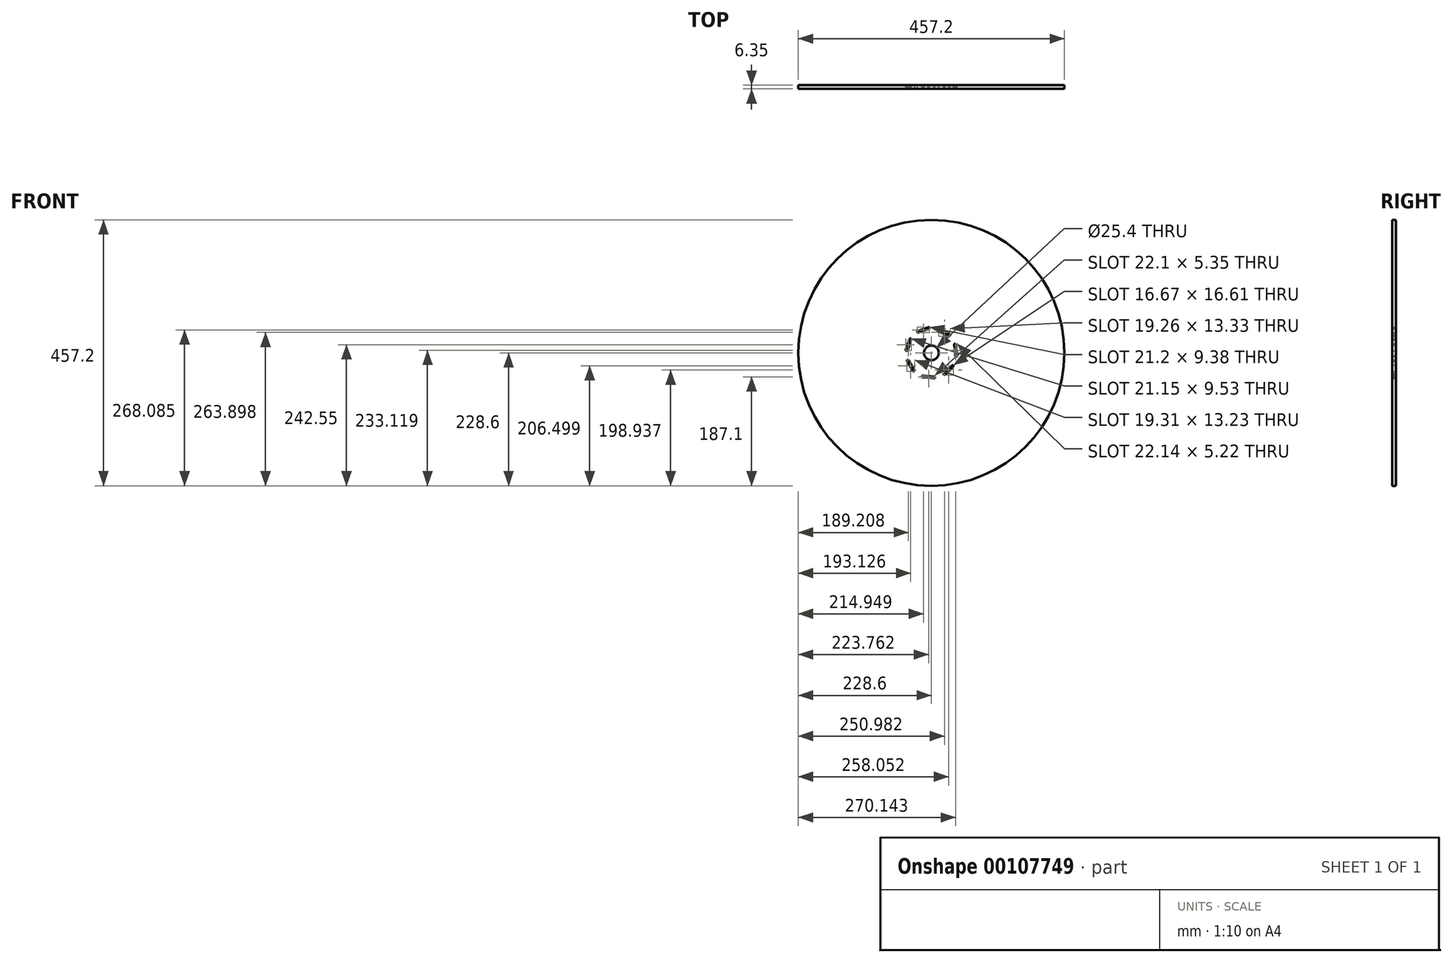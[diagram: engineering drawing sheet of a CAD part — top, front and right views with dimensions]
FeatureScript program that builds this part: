
annotation { "Feature Type Name" : "Feature", "Feature Type Description" : "" }
export const myFeature = defineFeature(function(context is Context, id is Id, definition is map)
    precondition{}
    {
        {
            var Q0;
            Q0=qCreatedBy(makeId("Front.planeOp"),FACE);
            var sketch = newSketch(context, id + "F0", { "sketchPlane" : qUnion([Q0])});
            skCircle(sketch, "E0", {"center": v(0, 0) * mm, "radius": 228.6 * mm});
            skSolve(sketch);
        }
        {
            var Q0;
            Q0 = qSketchRegion(id + "F0", true);
            extrude(context, id + "F1", {"entities" : qUnion([Q0]), "depth" : 6.35 * mm});
        }
        {
            var Q0;
            Q0=makeQuery(id+"F1.opExtrude","CAP_FACE",FACE,{"disambiguationData":[OSD([sQuery(id+"F0.wireOp",EDGE,"E0")])],"isStart":true});
            var sketch = newSketch(context, id + "F2", { "sketchPlane" : qUnion([Q0])});
            skLineSegment(sketch, "E1.8", {"start": v(-42.57, -4.96) * mm, "end": v(-42.57, -4.9) * mm});
            skArc(sketch, "E2", {"start": v(22.14, 34.88) * mm, "mid": v(24.17, 35.86) * mm, "end": v(23.18, 37.88) * mm});
            skArc(sketch, "E3", {"start": v(-30.7, 31.75) * mm, "mid": v(-31.88, 29.56) * mm, "end": v(-29.47, 28.92) * mm});
            skArc(sketch, "E4", {"start": v(-38.93, 13.83) * mm, "mid": v(-40.56, 15.59) * mm, "end": v(-42.08, 13.73) * mm});
            skArc(sketch, "E5", {"start": v(41.08, 4.44) * mm, "mid": v(43.1, 3.47) * mm, "end": v(44.07, 5.5) * mm});
            skArc(sketch, "E6", {"start": v(-44.15, -4.79) * mm, "mid": v(-42.6, -6.55) * mm, "end": v(-41, -4.83) * mm});
            skArc(sketch, "E7", {"start": v(-23.92, -37.35) * mm, "mid": v(-21.43, -37.38) * mm, "end": v(-21.98, -34.95) * mm});
            skArc(sketch, "E8", {"start": v(-4.65, -41.02) * mm, "mid": v(-6.2, -42.81) * mm, "end": v(-4.24, -44.15) * mm});
            skArc(sketch, "E9", {"start": v(29.08, -29.35) * mm, "mid": v(29.59, -31.54) * mm, "end": v(31.77, -31.03) * mm});
            skLineSegment(sketch, "E10.trimOffspring", {"start": v(3.05, 42.75) * mm, "end": v(3.05, 42.75) * mm});
            skLineSegment(sketch, "E11.trimOffspring", {"start": v(-42.55, -5.02) * mm, "end": v(-42.57, -4.96) * mm});
            skArc(sketch, "E12.trimOffspring", {"start": v(-36.2, -22.95) * mm, "mid": v(-36.2, -22.95) * mm, "end": v(-36.2, -22.96) * mm, "construction": true});
            skLineSegment(sketch, "E13", {"start": v(4.46, 41.03) * mm, "end": v(22.14, 34.88) * mm});
            skLineSegment(sketch, "E14", {"start": v(4.68, 44.2) * mm, "end": v(23.18, 37.88) * mm});
            skLineSegment(sketch, "E15", {"start": v(-31.73, 31.1) * mm, "end": v(-15.17, 41.74) * mm});
            skLineSegment(sketch, "E16", {"start": v(34.85, 22.12) * mm, "end": v(41.08, 4.44) * mm});
            skLineSegment(sketch, "E17", {"start": v(37.57, 23.76) * mm, "end": v(44.07, 5.5) * mm});
            skLineSegment(sketch, "E18", {"start": v(41.98, -14.6) * mm, "end": v(31.77, -31.03) * mm});
            skLineSegment(sketch, "E19", {"start": v(39.12, -13.24) * mm, "end": v(29.08, -29.35) * mm});
            skLineSegment(sketch, "E20", {"start": v(-4.65, -41.02) * mm, "end": v(14.13, -38.83) * mm});
            skLineSegment(sketch, "E21", {"start": v(13.8, -41.9) * mm, "end": v(15.24, -41.7) * mm});
            skLineSegment(sketch, "E22", {"start": v(-4.63, -44.2) * mm, "end": v(15.24, -41.7) * mm});
            skLineSegment(sketch, "E23", {"start": v(-23.62, -37.65) * mm, "end": v(-37.32, -24.07) * mm});
            skLineSegment(sketch, "E24", {"start": v(-21.98, -34.95) * mm, "end": v(-35.08, -21.82) * mm});
            skLineSegment(sketch, "E25", {"start": v(-44.15, -4.79) * mm, "end": v(-42.08, 13.73) * mm});
            skLineSegment(sketch, "E26", {"start": v(-41, -4.83) * mm, "end": v(-38.93, 13.83) * mm});
            skLineSegment(sketch, "E27", {"start": v(-29.47, 28.92) * mm, "end": v(-13.46, 39.06) * mm});
            skArc(sketch, "E28.trimOffspring", {"start": v(-13.46, 39.06) * mm, "mid": v(-12.98, 41.25) * mm, "end": v(-15.17, 41.74) * mm});
            skArc(sketch, "E29.trimOffspring", {"start": v(5.57, 43.9) * mm, "mid": v(3.15, 43.18) * mm, "end": v(4.46, 41.03) * mm});
            skArc(sketch, "E30.trimOffspring", {"start": v(37.78, 23.17) * mm, "mid": v(35.67, 24.44) * mm, "end": v(34.85, 22.12) * mm});
            skArc(sketch, "E31.trimOffspring", {"start": v(41.7, -15.06) * mm, "mid": v(41.43, -12.7) * mm, "end": v(39.12, -13.24) * mm});
            skArc(sketch, "E32.trimOffspring", {"start": v(13.74, -41.88) * mm, "mid": v(15.89, -40.6) * mm, "end": v(14.13, -38.83) * mm});
            skArc(sketch, "E33.trimOffspring", {"start": v(-35.08, -21.82) * mm, "mid": v(-37.33, -21.83) * mm, "end": v(-37.32, -24.07) * mm});
            skArc(sketch, "E34.trimOffspring", {"start": v(-42.71, -3.38) * mm, "mid": v(-42.72, -3.38) * mm, "end": v(-42.73, -3.38) * mm});
            skArc(sketch, "E35.trimOffspring", {"start": v(-42.57, -4.9) * mm, "mid": v(-42.56, -4.96) * mm, "end": v(-42.55, -5.02) * mm, "construction": true});
            skSolve(sketch);
        }
        {
            var Q0;
            Q0 = qSketchRegion(id + "F2", true);
            extrude(context, id + "F3", {"entities" : qUnion([Q0]), "operationType" : NewBodyOperationType.REMOVE, "endBound" : BoundingType.THROUGH_ALL, "oppositeDirection" : true, "depth" : 25.4 * mm});
        }
        {
            var Q0;
            Q0=makeQuery(id+"F1.opExtrude","CAP_FACE",FACE,{"disambiguationData":[OSD([sQuery(id+"F0.wireOp",EDGE,"E0")])],"isStart":false});
            var sketch = newSketch(context, id + "F4", { "sketchPlane" : qUnion([Q0])});
            skCircle(sketch, "E36", {"center": v(0, 0) * mm, "radius": 12.7 * mm});
            skSolve(sketch);
        }
        {
            var Q0;
            Q0 = qSketchRegion(id + "F4", true);
            extrude(context, id + "F5", {"entities" : qUnion([Q0]), "operationType" : NewBodyOperationType.REMOVE, "endBound" : BoundingType.THROUGH_ALL, "oppositeDirection" : true, "depth" : 25.4 * mm});
        }
    });
